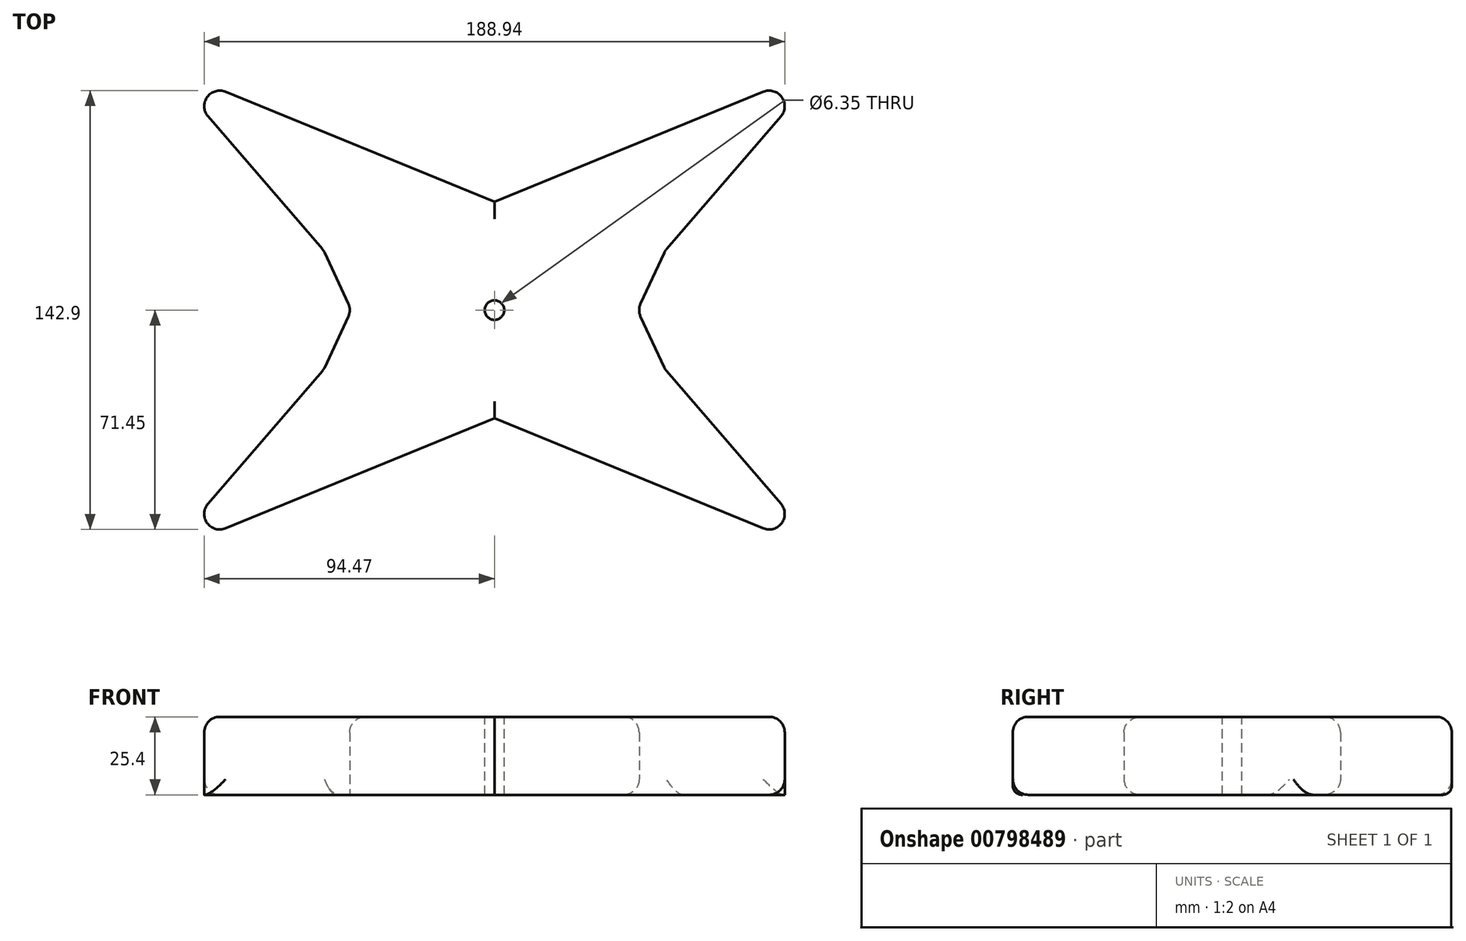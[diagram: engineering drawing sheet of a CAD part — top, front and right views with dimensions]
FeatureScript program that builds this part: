
annotation { "Feature Type Name" : "Feature", "Feature Type Description" : "" }
export const myFeature = defineFeature(function(context is Context, id is Id, definition is map)
    precondition{}
    {
        {
            var Q0;
            Q0=qCreatedBy(makeId("Top.planeOp"),FACE);
            var sketch = newSketch(context, id + "F0", { "sketchPlane" : qUnion([Q0])});
            skCircle(sketch, "E0", {"center": v(0, 0) * mm, "radius": 27.12 * mm});
            skCircle(sketch, "E1", {"center": v(0, 0) * mm, "radius": 35.25 * mm});
            skSolve(sketch);
        }
        {
            var Q0;
            Q0=qCreatedBy(makeId("Top.planeOp"),FACE);
            var sketch = newSketch(context, id + "F1", { "sketchPlane" : qUnion([Q0])});
            skLineSegment(sketch, "E2", {"start": v(0, -35.23) * mm, "end": v(107.05, -79.1) * mm});
            skLineSegment(sketch, "E3", {"start": v(107.05, -79.1) * mm, "end": v(55.56, -19.31) * mm});
            skLineSegment(sketch, "E4", {"start": v(55.56, -19.31) * mm, "end": v(46.58, 0) * mm});
            skLineSegment(sketch, "E5.MirrorCS", {"start": v(107.05, 79.1) * mm, "end": v(55.56, 19.31) * mm});
            skLineSegment(sketch, "E6.MirrorCS", {"start": v(55.56, 19.31) * mm, "end": v(46.58, 0) * mm});
            skLineSegment(sketch, "E7.MirrorCS", {"start": v(0, 35.23) * mm, "end": v(107.05, 79.1) * mm});
            skLineSegment(sketch, "E8.1.0", {"start": v(-55.56, -19.31) * mm, "end": v(-46.58, 0) * mm});
            skLineSegment(sketch, "E8.1.1", {"start": v(0, -35.23) * mm, "end": v(-107.05, -79.1) * mm});
            skLineSegment(sketch, "E8.1.2", {"start": v(0, 35.23) * mm, "end": v(-107.05, 79.1) * mm});
            skLineSegment(sketch, "E8.1.3", {"start": v(-107.05, 79.1) * mm, "end": v(-55.56, 19.31) * mm});
            skLineSegment(sketch, "E8.1.4", {"start": v(-55.56, 19.31) * mm, "end": v(-46.58, 0) * mm});
            skLineSegment(sketch, "E8.1.5", {"start": v(-107.05, -79.1) * mm, "end": v(-55.56, -19.31) * mm});
            skPoint(sketch, "E8.center", {"position": v(0, 0) * mm});
            skSolve(sketch);
        }
        {
            var Q0;
            Q0 = qSketchRegion(id + "F1", true);
            extrude(context, id + "F2", {"entities" : qUnion([Q0]), "depth" : 25.4 * mm, "offsetDistance" : 25.4 * mm});
        }
        {
            var Q0;
            Q0=makeQuery(id+"F2.opExtrude","CAP_EDGE",EDGE,{"disambiguationData":[OSD([sQuery(id+"F1.wireOp",EDGE,"E7.MirrorCS")])],"isStart":false});
            var Q1;
            Q1=makeQuery(id+"F2.opExtrude","CAP_EDGE",EDGE,{"disambiguationData":[OSD([sQuery(id+"F1.wireOp",EDGE,"E7.MirrorCS")])],"isStart":true});
            var Q2;
            Q2=makeQuery(id+"F2.opExtrude","SWEPT_EDGE",EDGE,{"disambiguationData":[OSD([sQuery(id+"F1.wireOp",EDGE,"E5.MirrorCS"),sQuery(id+"F1.wireOp",EDGE,"E7.MirrorCS")])]});
            var Q3;
            Q3=makeQuery(id+"F2.opExtrude","CAP_EDGE",EDGE,{"disambiguationData":[OSD([sQuery(id+"F1.wireOp",EDGE,"E5.MirrorCS")])],"isStart":false});
            var Q4;
            Q4=makeQuery(id+"F2.opExtrude","CAP_EDGE",EDGE,{"disambiguationData":[OSD([sQuery(id+"F1.wireOp",EDGE,"E6.MirrorCS")])],"isStart":false});
            var Q5;
            Q5=makeQuery(id+"F2.opExtrude","CAP_EDGE",EDGE,{"disambiguationData":[OSD([sQuery(id+"F1.wireOp",EDGE,"E4")])],"isStart":false});
            var Q6;
            Q6=makeQuery(id+"F2.opExtrude","CAP_EDGE",EDGE,{"disambiguationData":[OSD([sQuery(id+"F1.wireOp",EDGE,"E3")])],"isStart":false});
            var Q7;
            Q7=makeQuery(id+"F2.opExtrude","SWEPT_EDGE",EDGE,{"disambiguationData":[OSD([sQuery(id+"F1.wireOp",EDGE,"E2"),sQuery(id+"F1.wireOp",EDGE,"E3")])]});
            var Q8;
            Q8=makeQuery(id+"F2.opExtrude","CAP_EDGE",EDGE,{"disambiguationData":[OSD([sQuery(id+"F1.wireOp",EDGE,"E2")])],"isStart":true});
            var Q9;
            Q9=makeQuery(id+"F2.opExtrude","CAP_EDGE",EDGE,{"disambiguationData":[OSD([sQuery(id+"F1.wireOp",EDGE,"E2")])],"isStart":false});
            var Q10;
            Q10=makeQuery(id+"F2.opExtrude","CAP_EDGE",EDGE,{"disambiguationData":[OSD([sQuery(id+"F1.wireOp",EDGE,"E8.1.3")])],"isStart":false});
            var Q11;
            Q11=makeQuery(id+"F2.opExtrude","CAP_EDGE",EDGE,{"disambiguationData":[OSD([sQuery(id+"F1.wireOp",EDGE,"E8.1.2")])],"isStart":false});
            var Q12;
            Q12=makeQuery(id+"F2.opExtrude","CAP_EDGE",EDGE,{"disambiguationData":[OSD([sQuery(id+"F1.wireOp",EDGE,"E8.1.4")])],"isStart":false});
            var Q13;
            Q13=makeQuery(id+"F2.opExtrude","CAP_EDGE",EDGE,{"disambiguationData":[OSD([sQuery(id+"F1.wireOp",EDGE,"E8.1.0")])],"isStart":false});
            var Q14;
            Q14=makeQuery(id+"F2.opExtrude","CAP_EDGE",EDGE,{"disambiguationData":[OSD([sQuery(id+"F1.wireOp",EDGE,"E8.1.5")])],"isStart":false});
            var Q15;
            Q15=makeQuery(id+"F2.opExtrude","SWEPT_EDGE",EDGE,{"disambiguationData":[OSD([sQuery(id+"F1.wireOp",EDGE,"E8.1.0"),sQuery(id+"F1.wireOp",EDGE,"E8.1.5")])]});
            var Q16;
            Q16=makeQuery(id+"F2.opExtrude","SWEPT_EDGE",EDGE,{"disambiguationData":[OSD([sQuery(id+"F1.wireOp",EDGE,"E8.1.0"),sQuery(id+"F1.wireOp",EDGE,"E8.1.4")])]});
            var Q17;
            Q17=makeQuery(id+"F2.opExtrude","SWEPT_EDGE",EDGE,{"disambiguationData":[OSD([sQuery(id+"F1.wireOp",EDGE,"E8.1.3"),sQuery(id+"F1.wireOp",EDGE,"E8.1.4")])]});
            var Q18;
            Q18=makeQuery(id+"F2.opExtrude","CAP_EDGE",EDGE,{"disambiguationData":[OSD([sQuery(id+"F1.wireOp",EDGE,"E8.1.2")])],"isStart":true});
            var Q19;
            Q19=makeQuery(id+"F2.opExtrude","SWEPT_EDGE",EDGE,{"disambiguationData":[OSD([sQuery(id+"F1.wireOp",EDGE,"E8.1.2"),sQuery(id+"F1.wireOp",EDGE,"E8.1.3")])]});
            var Q20;
            Q20=makeQuery(id+"F2.opExtrude","CAP_EDGE",EDGE,{"disambiguationData":[OSD([sQuery(id+"F1.wireOp",EDGE,"E8.1.3")])],"isStart":true});
            var Q21;
            Q21=makeQuery(id+"F2.opExtrude","CAP_EDGE",EDGE,{"disambiguationData":[OSD([sQuery(id+"F1.wireOp",EDGE,"E8.1.1")])],"isStart":true});
            var Q22;
            Q22=makeQuery(id+"F2.opExtrude","SWEPT_EDGE",EDGE,{"disambiguationData":[OSD([sQuery(id+"F1.wireOp",EDGE,"E8.1.1"),sQuery(id+"F1.wireOp",EDGE,"E8.1.5")])]});
            var Q23;
            Q23=makeQuery(id+"F2.opExtrude","CAP_EDGE",EDGE,{"disambiguationData":[OSD([sQuery(id+"F1.wireOp",EDGE,"E8.1.1")])],"isStart":false});
            var Q24;
            Q24=makeQuery(id+"F2.opExtrude","CAP_EDGE",EDGE,{"disambiguationData":[OSD([sQuery(id+"F1.wireOp",EDGE,"E3")])],"isStart":true});
            var Q25;
            Q25=makeQuery(id+"F2.opExtrude","CAP_EDGE",EDGE,{"disambiguationData":[OSD([sQuery(id+"F1.wireOp",EDGE,"E4")])],"isStart":true});
            var Q26;
            Q26=makeQuery(id+"F2.opExtrude","SWEPT_EDGE",EDGE,{"disambiguationData":[OSD([sQuery(id+"F1.wireOp",EDGE,"E3"),sQuery(id+"F1.wireOp",EDGE,"E4")])]});
            var Q27;
            Q27=makeQuery(id+"F2.opExtrude","SWEPT_EDGE",EDGE,{"disambiguationData":[OSD([sQuery(id+"F1.wireOp",EDGE,"E4"),sQuery(id+"F1.wireOp",EDGE,"E6.MirrorCS")])]});
            var Q28;
            Q28=makeQuery(id+"F2.opExtrude","SWEPT_FACE",FACE,{"disambiguationData":[OSD([sQuery(id+"F1.wireOp",EDGE,"E6.MirrorCS")])]});
            fillet(context, id + "F3", {"entities" : qUnion([Q0, Q1, Q2, Q3, Q4, Q5, Q6, Q7, Q8, Q9, Q10, Q11, Q12, Q13, Q14, Q15, Q16, Q17, Q18, Q19, Q20, Q21, Q22, Q23, Q24, Q25, Q26, Q27, Q28]), "radius" : 5.08 * mm, "tangentPropagation" : true, "allowEdgeOverflow" : false});
        }
        {
            var Q0;
            Q0=sQuery(id+"F0.wireOp",EDGE,"E0");
            var Q1;
            Q1=sQuery(id+"F0.wireOp",EDGE,"E1");
            extrude(context, id + "F4", {"bodyType" : ToolBodyType.SURFACE, "surfaceEntities" : qUnion([Q0, Q1]), "depth" : 26.24 * mm, "offsetDistance" : 25.4 * mm});
        }
        {
            var Q0;
            Q0=makeQuery(id+"F2.opExtrude","CAP_FACE",FACE,{"disambiguationData":[OSD([sQuery(id+"F1.wireOp",EDGE,"E2"),sQuery(id+"F1.wireOp",EDGE,"E3"),sQuery(id+"F1.wireOp",EDGE,"E4"),sQuery(id+"F1.wireOp",EDGE,"E5.MirrorCS"),sQuery(id+"F1.wireOp",EDGE,"E6.MirrorCS"),sQuery(id+"F1.wireOp",EDGE,"E7.MirrorCS"),sQuery(id+"F1.wireOp",EDGE,"E8.1.0"),sQuery(id+"F1.wireOp",EDGE,"E8.1.1"),sQuery(id+"F1.wireOp",EDGE,"E8.1.2"),sQuery(id+"F1.wireOp",EDGE,"E8.1.3"),sQuery(id+"F1.wireOp",EDGE,"E8.1.4"),sQuery(id+"F1.wireOp",EDGE,"E8.1.5")])],"isStart":false});
            var sketch = newSketch(context, id + "F5", { "sketchPlane" : qUnion([Q0])});
            skCircle(sketch, "E9", {"center": v(0, 0) * mm, "radius": 29.74 * mm});
            skSolve(sketch);
        }
        {
            var Q0;
            Q0=sQuery(id+"F5.wireOp",VERTEX,"E9.center");
            var Q1;
            Q1=makeQuery(id+"F2.opExtrude","SWEPT_BODY",BODY,{"disambiguationData":[OSD([sQuery(id+"F1.wireOp",EDGE,"E2"),sQuery(id+"F1.wireOp",EDGE,"E3"),sQuery(id+"F1.wireOp",EDGE,"E4"),sQuery(id+"F1.wireOp",EDGE,"E5.MirrorCS"),sQuery(id+"F1.wireOp",EDGE,"E6.MirrorCS"),sQuery(id+"F1.wireOp",EDGE,"E7.MirrorCS"),sQuery(id+"F1.wireOp",EDGE,"E8.1.0"),sQuery(id+"F1.wireOp",EDGE,"E8.1.1"),sQuery(id+"F1.wireOp",EDGE,"E8.1.2"),sQuery(id+"F1.wireOp",EDGE,"E8.1.3"),sQuery(id+"F1.wireOp",EDGE,"E8.1.4"),sQuery(id+"F1.wireOp",EDGE,"E8.1.5")])]});
            hole(context, id + "F6", {"style" : HoleStyle.SIMPLE, "endStyle" : HoleEndStyle.THROUGH, "holeDiameter" : 6.35 * mm, "majorDiameter" : 6.35 * mm, "isTappedThrough" : true, "tappedDepth" : 12.7 * mm, "tapClearance" : 3, "locations" : qUnion([Q0]), "scope" : qUnion([Q1])});
        }
    });
